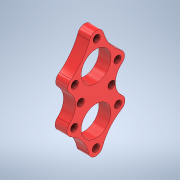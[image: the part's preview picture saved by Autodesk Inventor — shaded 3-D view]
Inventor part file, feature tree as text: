
AUTODESK INVENTOR PART (.ipt)
format: ipt  version: 2021 (Build 250183000, 183)  size: 193,024 bytes
history: native  units: in
note: dims shown in document units (in); Inventor stores cm internally (conversion verified against a paired STEP export)
features: sketch x2, extrude x1
ambient origin geometry x8: Origin, YZ Plane, XZ Plane, XY Plane, X Axis, Y Axis, Z Axis, Center Point
bodies: Solid1 (feature_tree)
feature tree (3):
  sketch  "Sketch1"  dims[d1=0.9843in d2=1.4961in]
  extrude  "Extrusion1"  Depth=1.4961in
  sketch  "Sketch2"  dims[d3=1.5748in d4=0.9843in d6=0.4724in d7=0.2362in d12=0.4724in d13=0.4724in d14=1.4961in d15=0.4724in d16=0.4724in d17=0.5118in d18=0.5118in d21=0.4724in d22=0.2362in d23=0.2362in d24=0.2362in d25=0.2362in d26=0.2362in d27=0.2362in d28=0.2362in d29=0.5906in d30=0.5906in d31=1.4671in d34=1.4323in d35=0.3937in d36=0.0in]
